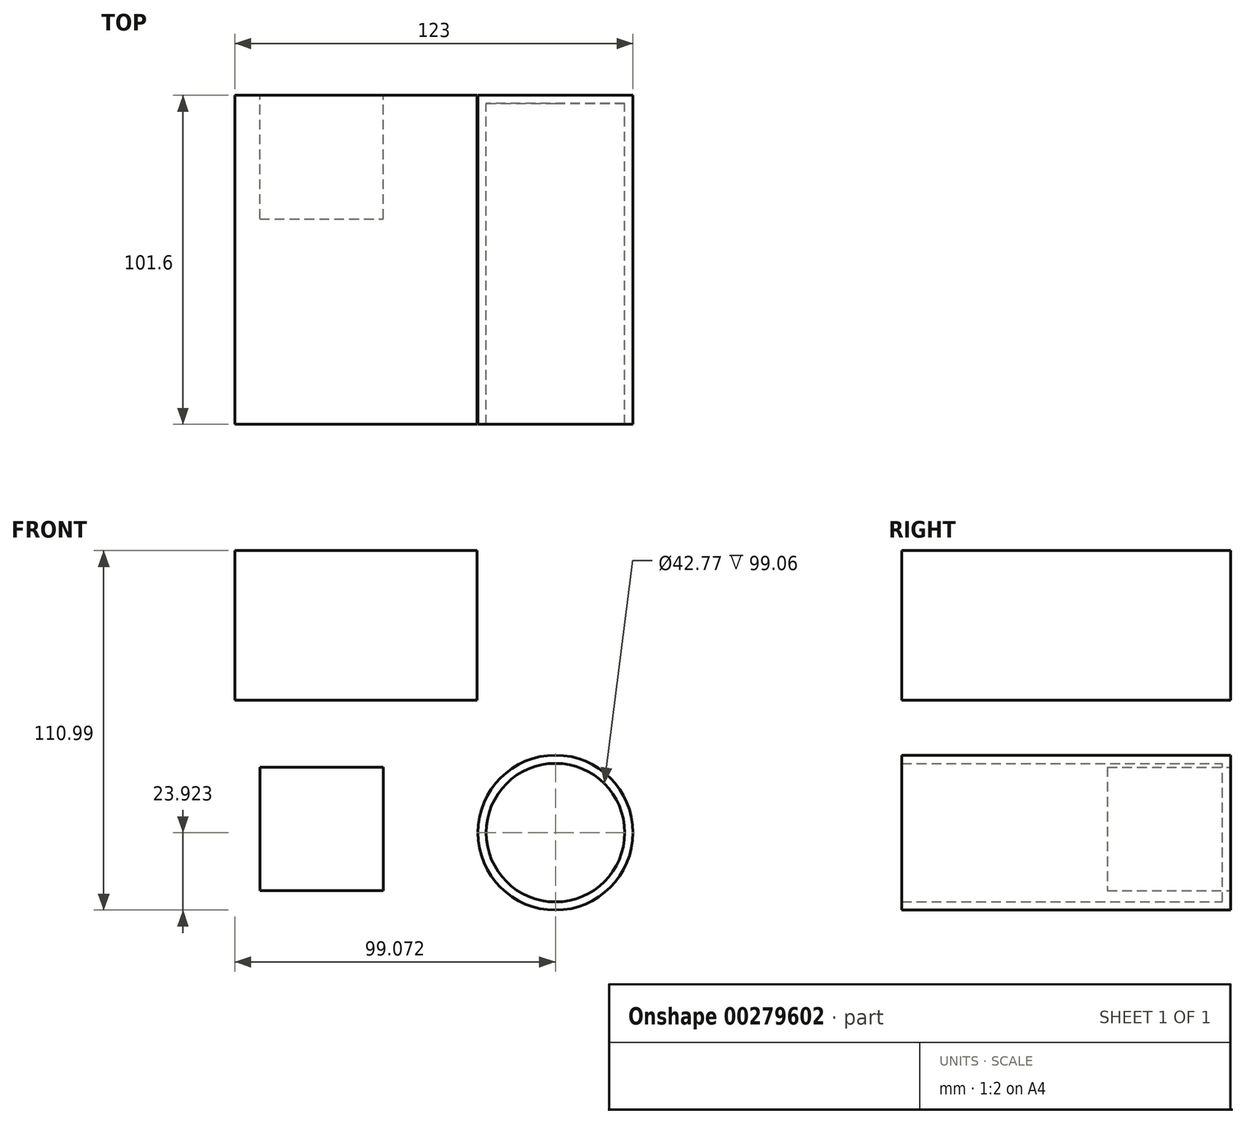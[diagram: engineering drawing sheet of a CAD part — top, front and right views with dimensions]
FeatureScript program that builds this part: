
annotation { "Feature Type Name" : "Feature", "Feature Type Description" : "" }
export const myFeature = defineFeature(function(context is Context, id is Id, definition is map)
    precondition{}
    {
        {
            var Q0;
            Q0=qCreatedBy(makeId("Front.planeOp"),FACE);
            var sketch = newSketch(context, id + "F0", { "sketchPlane" : qUnion([Q0])});
            skLineSegment(sketch, "E0.bottom", {"start": v(-68.48, 56.24) * mm, "end": v(6.35, 56.24) * mm});
            skLineSegment(sketch, "E0.top", {"start": v(-68.48, 10.12) * mm, "end": v(6.35, 10.12) * mm});
            skLineSegment(sketch, "E0.left", {"start": v(-68.48, 56.24) * mm, "end": v(-68.48, 10.12) * mm});
            skLineSegment(sketch, "E0.right", {"start": v(6.35, 56.24) * mm, "end": v(6.35, 10.12) * mm});
            skSolve(sketch);
        }
        {
            var Q0;
            Q0=qCreatedBy(makeId("Front.planeOp"),FACE);
            var sketch = newSketch(context, id + "F1", { "sketchPlane" : qUnion([Q0])});
            skLineSegment(sketch, "E1.bottom", {"start": v(-60.71, -10.59) * mm, "end": v(-22.6, -10.59) * mm});
            skLineSegment(sketch, "E1.top", {"start": v(-60.71, -48.71) * mm, "end": v(-22.6, -48.71) * mm});
            skLineSegment(sketch, "E1.left", {"start": v(-60.71, -10.59) * mm, "end": v(-60.71, -48.71) * mm});
            skLineSegment(sketch, "E1.right", {"start": v(-22.6, -10.59) * mm, "end": v(-22.6, -48.71) * mm});
            skPoint(sketch, "E1.middle", {"position": v(-41.65, -29.65) * mm});
            skSolve(sketch);
        }
        {
            var Q0;
            Q0=makeQuery(id+"F0.imprint","IMPRINT",FACE,{"disambiguationData":[TD([[makeQuery(id+"F0.imprint","IMPRINT",EDGE,{"derivedFrom":sQuery(id+"F0.wireOp",EDGE,"E0.bottom")}),-1.0]])]});
            extrude(context, id + "F2", {"entities" : qUnion([Q0]), "depth" : 101.6 * mm});
        }
        {
            var Q0;
            Q0=makeQuery(id+"F1.imprint","IMPRINT",FACE,{"disambiguationData":[TD([[makeQuery(id+"F1.imprint","IMPRINT",EDGE,{"derivedFrom":sQuery(id+"F1.wireOp",EDGE,"E1.bottom")}),-1.0]])]});
            extrude(context, id + "F3", {"entities" : qUnion([Q0]), "depth" : 38.13 * mm});
        }
        {
            var Q0;
            Q0=qCreatedBy(makeId("Front.planeOp"),FACE);
            var sketch = newSketch(context, id + "F4", { "sketchPlane" : qUnion([Q0])});
            skCircle(sketch, "E2", {"center": v(30.6, -30.83) * mm, "radius": 23.93 * mm});
            skSolve(sketch);
        }
        {
            var Q0;
            Q0=makeQuery(id+"F4.imprint","IMPRINT",FACE,{"disambiguationData":[TD([[makeQuery(id+"F4.imprint","IMPRINT",EDGE,{"derivedFrom":sQuery(id+"F4.wireOp",EDGE,"E2")}),1.0]])]});
            extrude(context, id + "F5", {"entities" : qUnion([Q0]), "depth" : 101.6 * mm});
        }
        {
            var Q0;
            Q0=makeQuery(id+"F5.opExtrude","CAP_FACE",FACE,{"disambiguationData":[OSD([sQuery(id+"F4.wireOp",EDGE,"E2")])],"isStart":false});
            shell(context, id + "F6", {"entities" : qUnion([Q0]), "thickness" : 2.54 * mm});
        }
    });
